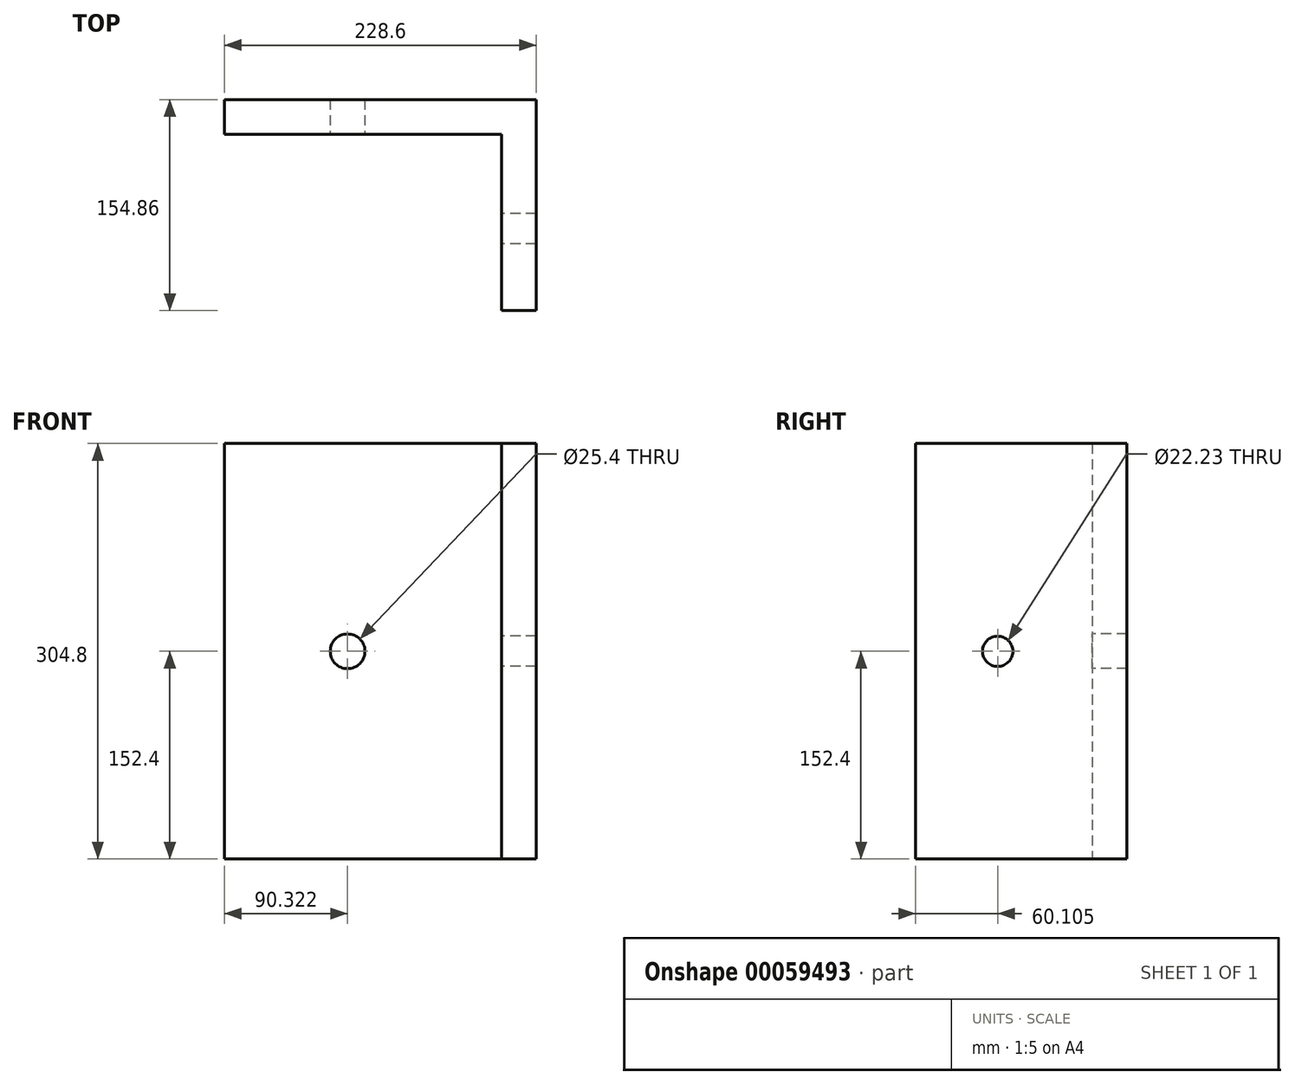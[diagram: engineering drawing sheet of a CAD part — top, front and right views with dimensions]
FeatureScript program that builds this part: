
annotation { "Feature Type Name" : "Feature", "Feature Type Description" : "" }
export const myFeature = defineFeature(function(context is Context, id is Id, definition is map)
    precondition{}
    {
        {
            var Q0;
            Q0=qCreatedBy(makeId("Front.planeOp"),FACE);
            var sketch = newSketch(context, id + "F0", { "sketchPlane" : qUnion([Q0])});
            skLineSegment(sketch, "E0.rect.bottom", {"start": v(101.6, 152.4) * mm, "end": v(-101.6, 152.4) * mm});
            skLineSegment(sketch, "E0.rect.top", {"start": v(101.6, -152.4) * mm, "end": v(-101.6, -152.4) * mm});
            skLineSegment(sketch, "E0.rect.left", {"start": v(101.6, 152.4) * mm, "end": v(101.6, -152.4) * mm});
            skLineSegment(sketch, "E0.rect.right", {"start": v(-101.6, 152.4) * mm, "end": v(-101.6, -152.4) * mm});
            skSolve(sketch);
        }
        {
            var Q0;
            Q0=makeQuery(id+"F0.imprint","IMPRINT",FACE,{"disambiguationData":[TD([[makeQuery(id+"F0.imprint","IMPRINT",EDGE,{"derivedFrom":sQuery(id+"F0.wireOp",EDGE,"E0.rect.bottom")}),1.0]])]});
            extrude(context, id + "F1", {"entities" : qUnion([Q0]), "oppositeDirection" : true, "depth" : 25.4 * mm});
        }
        {
            var Q0;
            Q0=makeQuery(id+"F1.opExtrude","SWEPT_FACE",FACE,{"disambiguationData":[OSD([sQuery(id+"F0.wireOp",EDGE,"E0.rect.left")])]});
            var sketch = newSketch(context, id + "F2", { "sketchPlane" : qUnion([Q0])});
            skLineSegment(sketch, "E1.bottom", {"start": v(25.4, 152.4) * mm, "end": v(-129.46, 152.4) * mm});
            skLineSegment(sketch, "E1.top", {"start": v(25.4, -152.4) * mm, "end": v(-129.46, -152.4) * mm});
            skLineSegment(sketch, "E1.left", {"start": v(25.4, 152.4) * mm, "end": v(25.4, -152.4) * mm});
            skLineSegment(sketch, "E1.right", {"start": v(-129.46, 152.4) * mm, "end": v(-129.46, -152.4) * mm});
            skLineSegment(sketch, "E2", {"start": v(-27.86, -152.4) * mm, "end": v(-27.86, 152.4) * mm, "construction": true});
            skSolve(sketch);
        }
        {
            var Q0;
            {var subQ2=sQuery(id+"F2.wireOp",EDGE,"E1.left");Q0=makeQuery(id+"F2.imprint","IMPRINT",FACE,{"disambiguationData":[TD([[makeQuery(id+"F2.imprint","IMPRINT",EDGE,{"derivedFrom":subQ2}),-1.0]])]});}
            var Q1;
            {var subQ2=sQuery(id+"F2.wireOp",EDGE,"E1.right");Q1=makeQuery(id+"F2.imprint","IMPRINT",FACE,{"disambiguationData":[TD([[makeQuery(id+"F2.imprint","IMPRINT",EDGE,{"derivedFrom":subQ2}),1.0]])]});}
            extrude(context, id + "F3", {"entities" : qUnion([Q0, Q1]), "operationType" : NewBodyOperationType.ADD, "depth" : 25.4 * mm});
        }
        {
            var Q0;
            Q0=makeQuery(id+"F1.opExtrude","CAP_FACE",FACE,{"disambiguationData":[OSD([sQuery(id+"F0.wireOp",EDGE,"E0.rect.bottom"),sQuery(id+"F0.wireOp",EDGE,"E0.rect.top"),sQuery(id+"F0.wireOp",EDGE,"E0.rect.left"),sQuery(id+"F0.wireOp",EDGE,"E0.rect.right")])],"isStart":true});
            var sketch = newSketch(context, id + "F4", { "sketchPlane" : qUnion([Q0])});
            skCircle(sketch, "E3", {"center": v(-11.28, 0) * mm, "radius": 12.7 * mm});
            skLineSegment(sketch, "E4", {"start": v(-11.28, -152.4) * mm, "end": v(-11.28, 152.4) * mm, "construction": true});
            skCircle(sketch, "E5", {"center": v(-11.28, 0) * mm, "radius": 76.67 * mm, "construction": true});
            skLineSegment(sketch, "E6", {"start": v(65.4, -152.4) * mm, "end": v(65.4, 152.4) * mm, "construction": true});
            skSolve(sketch);
        }
        {
            var Q0;
            Q0 = qSketchRegion(id + "F4", true);
            extrude(context, id + "F5", {"entities" : qUnion([Q0]), "operationType" : NewBodyOperationType.REMOVE, "endBound" : BoundingType.THROUGH_ALL, "oppositeDirection" : true, "depth" : 25.4 * mm});
        }
        {
            var Q0;
            Q0=makeQuery(id+"F3.opExtrude","CAP_FACE",FACE,{"disambiguationData":[OSD([sQuery(id+"F2.wireOp",EDGE,"E1.bottom"),sQuery(id+"F2.wireOp",EDGE,"E1.top"),sQuery(id+"F2.wireOp",EDGE,"E1.left"),sQuery(id+"F2.wireOp",EDGE,"E1.right")])],"isStart":true});
            var sketch = newSketch(context, id + "F6", { "sketchPlane" : qUnion([Q0])});
            skCircle(sketch, "E7", {"center": v(69.35, 0) * mm, "radius": 11.11 * mm});
            skCircle(sketch, "E8", {"center": v(69.35, 0) * mm, "radius": 28.8 * mm, "construction": true});
            skLineSegment(sketch, "E9", {"start": v(40.56, -152.4) * mm, "end": v(40.56, 152.4) * mm, "construction": true});
            skSolve(sketch);
        }
        {
            var Q0;
            Q0 = qSketchRegion(id + "F6", true);
            extrude(context, id + "F7", {"entities" : qUnion([Q0]), "operationType" : NewBodyOperationType.REMOVE, "endBound" : BoundingType.THROUGH_ALL, "oppositeDirection" : true, "depth" : 25.4 * mm});
        }
    });
